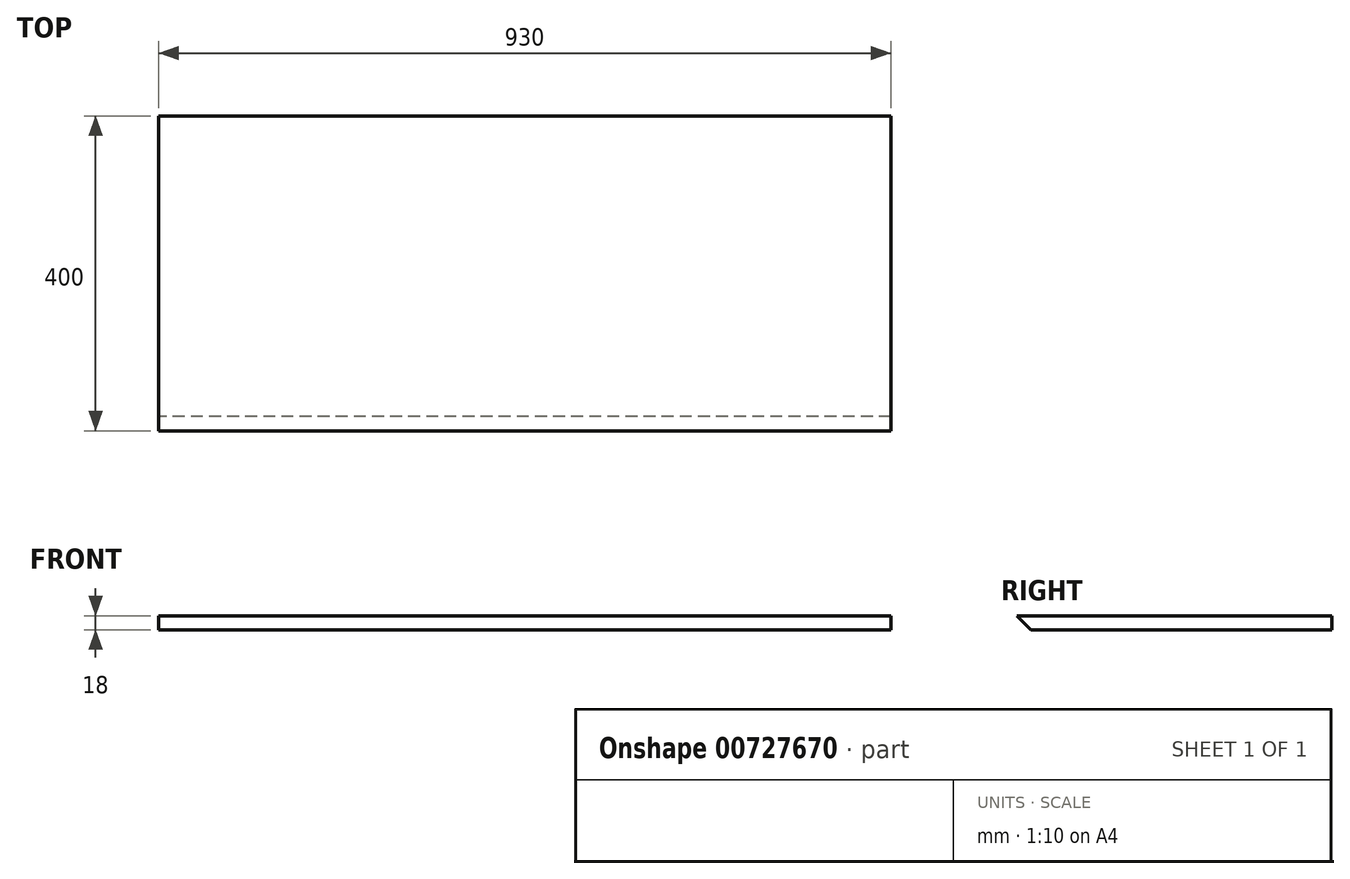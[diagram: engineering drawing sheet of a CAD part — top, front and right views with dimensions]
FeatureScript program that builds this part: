
annotation { "Feature Type Name" : "Feature", "Feature Type Description" : "" }
export const myFeature = defineFeature(function(context is Context, id is Id, definition is map)
    precondition{}
    {
        {
            var Q0;
            Q0=qCreatedBy(makeId("Top.planeOp"),FACE);
            var sketch = newSketch(context, id + "F0", { "sketchPlane" : qUnion([Q0])});
            skLineSegment(sketch, "E0.bottom", {"start": v(-465, 200) * mm, "end": v(465, 200) * mm});
            skLineSegment(sketch, "E0.top", {"start": v(-465, -200) * mm, "end": v(465, -200) * mm});
            skLineSegment(sketch, "E0.left", {"start": v(-465, 200) * mm, "end": v(-465, -200) * mm});
            skLineSegment(sketch, "E0.right", {"start": v(465, 200) * mm, "end": v(465, -200) * mm});
            skLineSegment(sketch, "E1", {"start": v(-465, 200) * mm, "end": v(465, -200) * mm, "construction": true});
            skSolve(sketch);
        }
        {
            var Q0;
            Q0 = qSketchRegion(id + "F0", true);
            extrude(context, id + "F1", {"entities" : qUnion([Q0]), "oppositeDirection" : true, "depth" : 18 * mm, "offsetDistance" : 25 * mm});
        }
        {
            var Q0;
            Q0=makeQuery(id+"F1.opExtrude","CAP_EDGE",EDGE,{"disambiguationData":[OSD([sQuery(id+"F0.wireOp",EDGE,"E0.top")])],"isStart":false});
            chamfer(context, id + "F2", {"entities" : qUnion([Q0]), "width" : 18 * mm, "tangentPropagation" : true});
        }
    });
